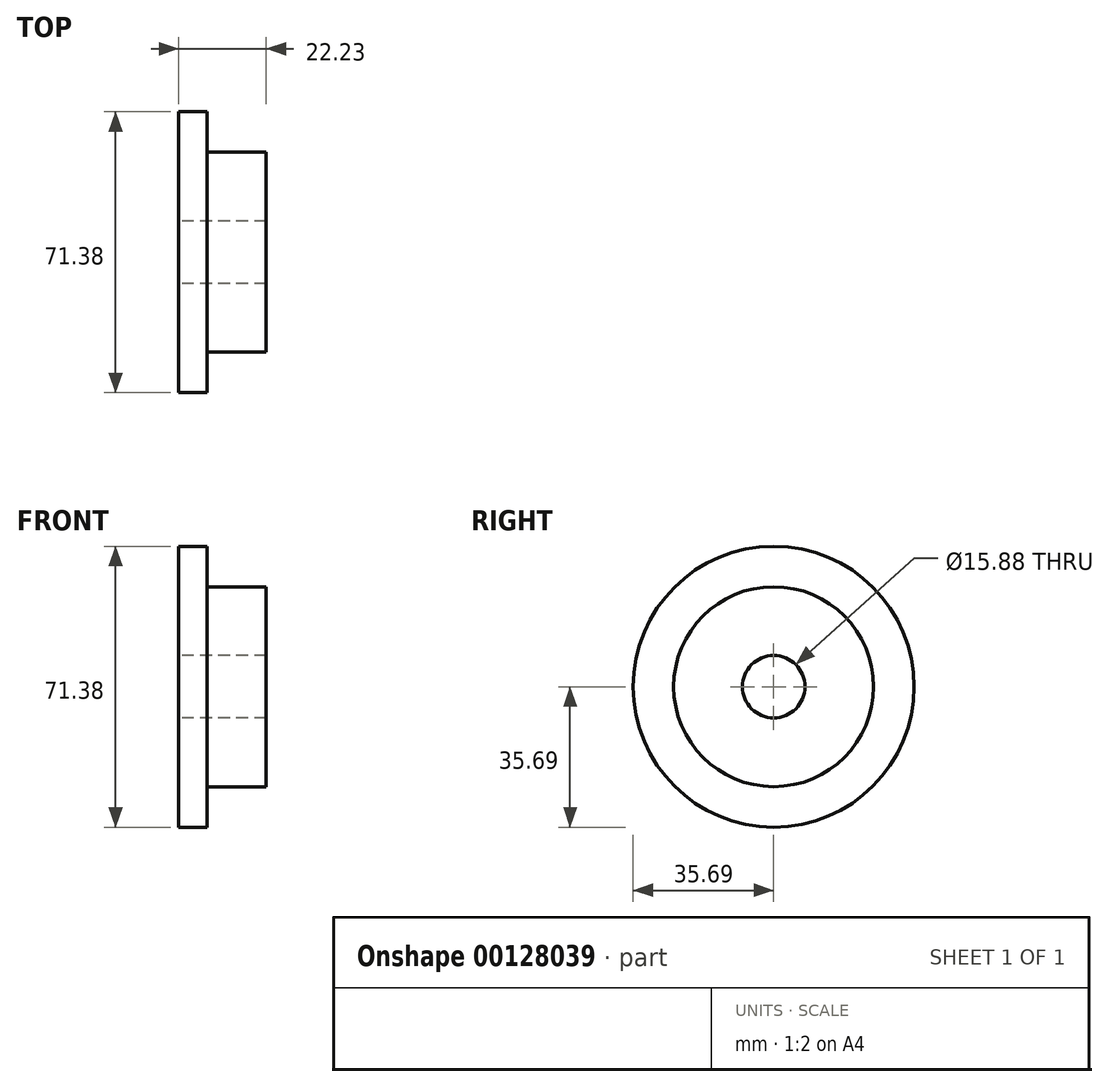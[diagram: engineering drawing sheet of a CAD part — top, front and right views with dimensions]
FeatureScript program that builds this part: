
annotation { "Feature Type Name" : "Feature", "Feature Type Description" : "" }
export const myFeature = defineFeature(function(context is Context, id is Id, definition is map)
    precondition{}
    {
        {
            var Q0;
            Q0=qCreatedBy(makeId("Front.planeOp"),FACE);
            var sketch = newSketch(context, id + "F0", { "sketchPlane" : qUnion([Q0])});
            skLineSegment(sketch, "E0", {"start": v(0, 0) * mm, "end": v(26.13, 0) * mm, "construction": true});
            skLineSegment(sketch, "E1.bottom", {"start": v(0, 7.94) * mm, "end": v(7.21, 7.94) * mm});
            skLineSegment(sketch, "E1.top", {"start": v(0, 35.69) * mm, "end": v(7.21, 35.69) * mm});
            skLineSegment(sketch, "E1.left", {"start": v(0, 7.94) * mm, "end": v(0, 35.69) * mm});
            skLineSegment(sketch, "E1.right", {"start": v(7.21, 7.94) * mm, "end": v(7.21, 35.69) * mm});
            skLineSegment(sketch, "E2.bottom", {"start": v(0, 7.94) * mm, "end": v(22.23, 7.94) * mm});
            skLineSegment(sketch, "E2.top", {"start": v(0, 25.4) * mm, "end": v(22.22, 25.4) * mm});
            skLineSegment(sketch, "E2.left", {"start": v(0, 7.94) * mm, "end": v(0, 25.4) * mm});
            skLineSegment(sketch, "E2.right", {"start": v(22.23, 7.94) * mm, "end": v(22.22, 25.4) * mm});
            skLineSegment(sketch, "E3.bottom", {"start": v(0, -7.94) * mm, "end": v(22.23, -7.94) * mm});
            skLineSegment(sketch, "E3.top", {"start": v(0, -25.4) * mm, "end": v(22.23, -25.4) * mm});
            skLineSegment(sketch, "E3.left", {"start": v(0, -7.94) * mm, "end": v(0, -25.4) * mm});
            skLineSegment(sketch, "E3.right", {"start": v(22.23, -7.94) * mm, "end": v(22.23, -25.4) * mm});
            skLineSegment(sketch, "E4.bottom", {"start": v(0, -7.94) * mm, "end": v(7.21, -7.94) * mm});
            skLineSegment(sketch, "E4.top", {"start": v(0, -35.69) * mm, "end": v(7.21, -35.69) * mm});
            skLineSegment(sketch, "E4.left", {"start": v(0, -7.94) * mm, "end": v(0, -35.69) * mm});
            skLineSegment(sketch, "E4.right", {"start": v(7.21, -7.94) * mm, "end": v(7.21, -35.69) * mm});
            skSolve(sketch);
        }
        {
            var Q0;
            {var subQ0=sQuery(id+"F0.wireOp",EDGE,"E3.bottom");Q0=makeQuery(id+"F0.imprint","IMPRINT",FACE,{"disambiguationData":[TD([[makeQuery(id+"F0.imprint","IMPRINT",EDGE,{"derivedFrom":subQ0}),-1.0]])]});}
            var Q1;
            {var subQ5=sQuery(id+"F0.wireOp",EDGE,"E4.bottom");Q1=makeQuery(id+"F0.imprint","IMPRINT",FACE,{"disambiguationData":[TD([[makeQuery(id+"F0.imprint","IMPRINT",EDGE,{"derivedFrom":subQ5}),-1.0]])]});}
            var Q2;
            {var subQ5=sQuery(id+"F0.wireOp",EDGE,"E4.top");Q2=makeQuery(id+"F0.imprint","IMPRINT",FACE,{"disambiguationData":[TD([[makeQuery(id+"F0.imprint","IMPRINT",EDGE,{"derivedFrom":subQ5}),1.0]])]});}
            var Q3;
            Q3=sQuery(id+"F0.wireOp",EDGE,"E0");
            revolve(context, id + "F1", {"entities" : qUnion([Q0, Q1, Q2]), "axis" : qUnion([Q3]), "revolveType" : RevolveType.FULL});
        }
    });
